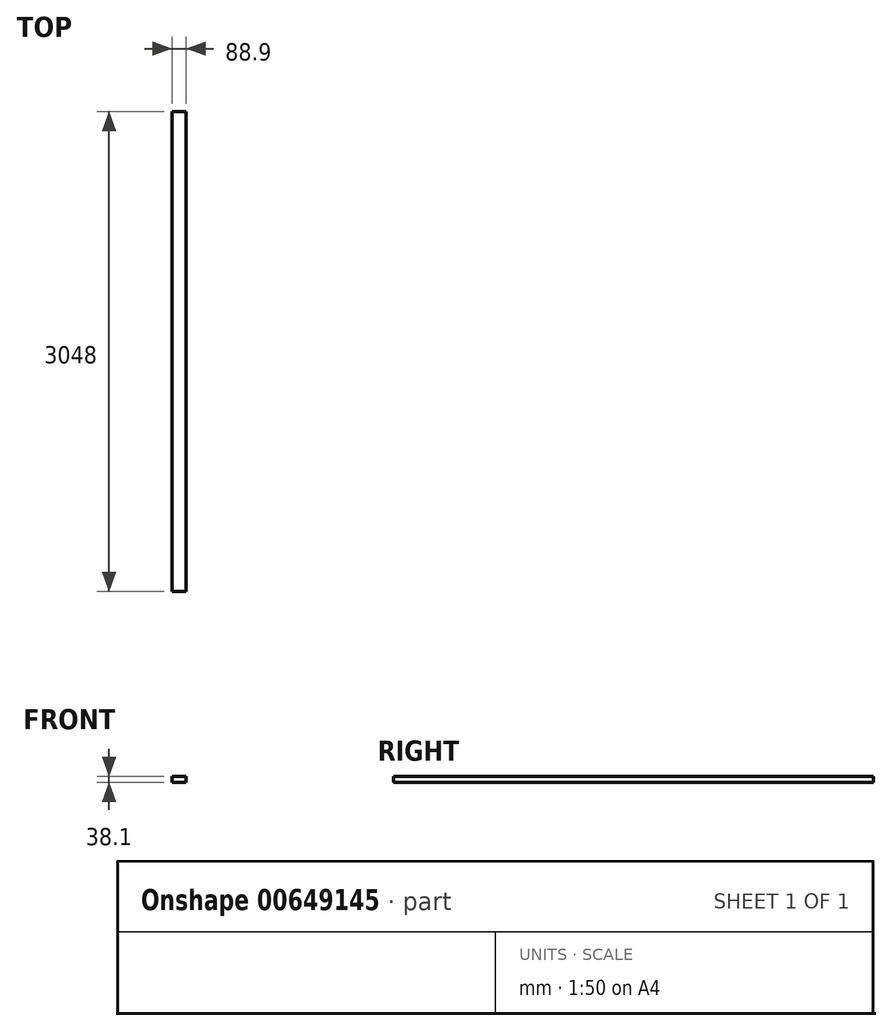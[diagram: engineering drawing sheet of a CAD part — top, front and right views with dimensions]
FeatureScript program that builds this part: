
annotation { "Feature Type Name" : "Feature", "Feature Type Description" : "" }
export const myFeature = defineFeature(function(context is Context, id is Id, definition is map)
    precondition{}
    {
        {
            var Q0;
            Q0=qCreatedBy(makeId("Front.planeOp"),FACE);
            var sketch = newSketch(context, id + "F0", { "sketchPlane" : qUnion([Q0])});
            skLineSegment(sketch, "E0.bottom", {"start": v(0, 0) * mm, "end": v(88.9, 0) * mm});
            skLineSegment(sketch, "E0.top", {"start": v(0, 38.1) * mm, "end": v(88.9, 38.1) * mm});
            skLineSegment(sketch, "E0.left", {"start": v(0, 0) * mm, "end": v(0, 38.1) * mm});
            skLineSegment(sketch, "E0.right", {"start": v(88.9, 0) * mm, "end": v(88.9, 38.1) * mm});
            skSolve(sketch);
        }
        {
            var Q0;
            Q0=qSketchRegion(id+"F0",true);
            extrude(context, id + "F1", {"entities" : qUnion([Q0]), "depth" : 3048 * mm, "offsetDistance" : 25.4 * mm});
        }
    });
